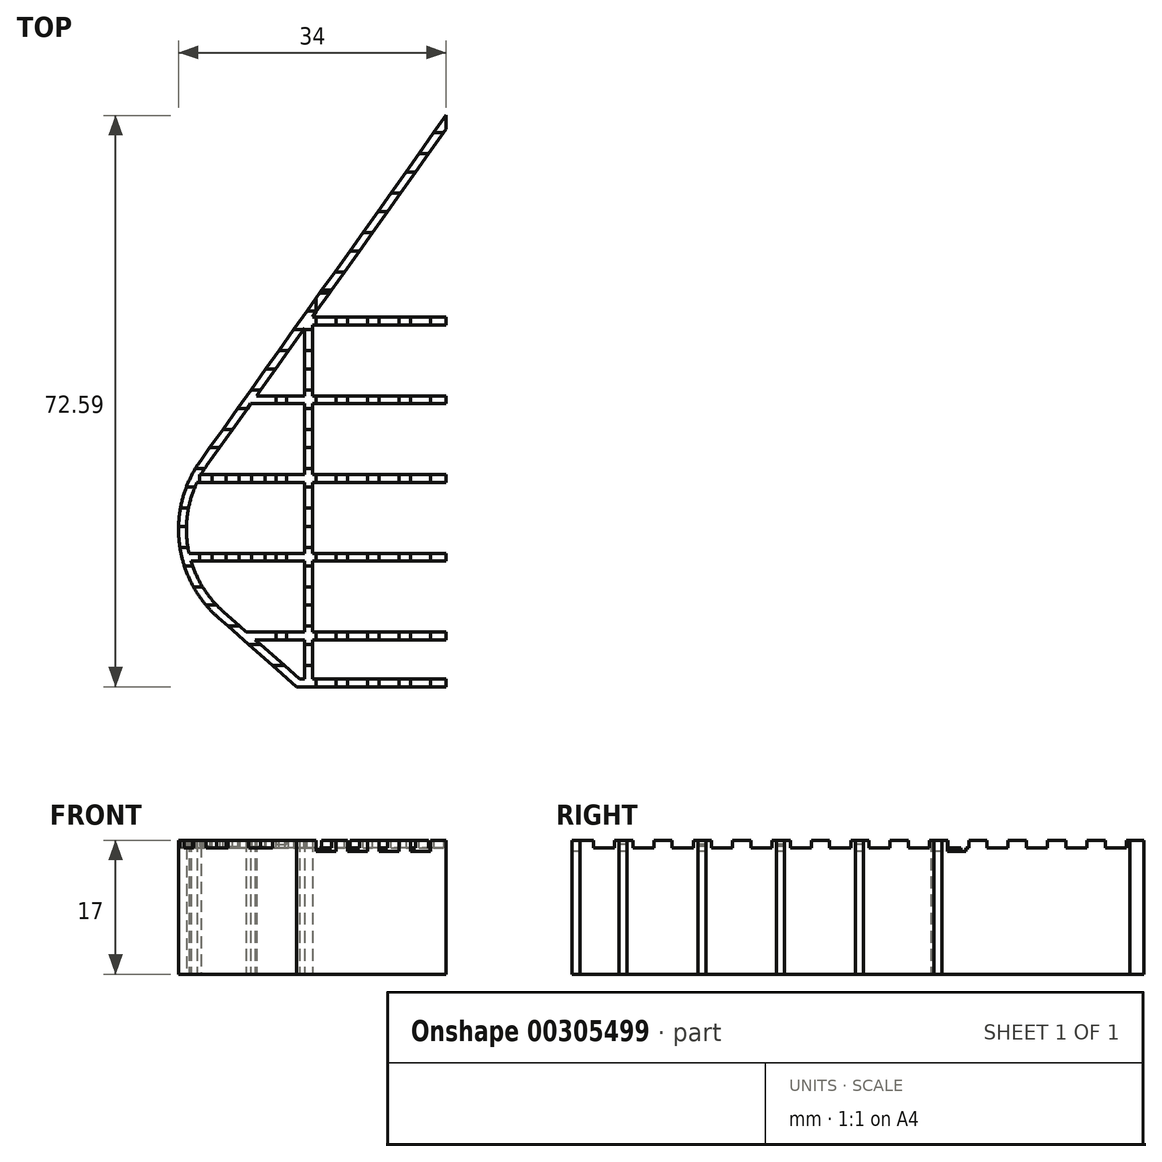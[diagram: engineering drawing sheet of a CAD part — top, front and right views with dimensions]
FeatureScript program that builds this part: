
annotation { "Feature Type Name" : "Feature", "Feature Type Description" : "" }
export const myFeature = defineFeature(function(context is Context, id is Id, definition is map)
    precondition{}
    {
        {
            var Q0;
            Q0=qCreatedBy(makeId("Top.planeOp"),FACE);
            var sketch = newSketch(context, id + "F0", { "sketchPlane" : qUnion([Q0])});
            skLineSegment(sketch, "E0.MirrorCS", {"start": v(-52.18, -20) * mm, "end": v(-53.18, -20) * mm, "construction": true});
            skLineSegment(sketch, "E1.MirrorCS", {"start": v(-53.18, -19) * mm, "end": v(-53.18, -20) * mm});
            skLineSegment(sketch, "E2.MirrorCS", {"start": v(-71.18, -19) * mm, "end": v(-71.8, -19) * mm});
            skLineSegment(sketch, "E3.MirrorCS", {"start": v(-53.18, 52.6) * mm, "end": v(-53.18, 50.87) * mm});
            skLineSegment(sketch, "E4.MirrorCS", {"start": v(-53.18, -19) * mm, "end": v(-70.18, -19) * mm, "construction": true});
            skLineSegment(sketch, "E5.MirrorCS", {"start": v(-71.18, 25.56) * mm, "end": v(-77.3, 16.97) * mm});
            skLineSegment(sketch, "E6.MirrorCS", {"start": v(-70.18, -19) * mm, "end": v(-70.18, -14.03) * mm});
            skLineSegment(sketch, "E7.MirrorCS", {"start": v(-53.18, 50.87) * mm, "end": v(-70.18, 26.97) * mm});
            skLineSegment(sketch, "E8.MirrorCS", {"start": v(-72.18, 0) * mm, "end": v(-52.18, 0) * mm, "construction": true});
            skLineSegment(sketch, "E9.MirrorCS", {"start": v(-52.18, 0) * mm, "end": v(-52.18, 54) * mm, "construction": true});
            skLineSegment(sketch, "E10.MirrorCS", {"start": v(-53.18, -19) * mm, "end": v(-53.18, 56.1) * mm, "construction": true});
            skLineSegment(sketch, "E11.MirrorCS", {"start": v(-52.18, 0) * mm, "end": v(-52.18, -20) * mm, "construction": true});
            skLineSegment(sketch, "E12.MirrorCS", {"start": v(-53.18, -19) * mm, "end": v(-70.18, -19) * mm});
            skLineSegment(sketch, "E13.MirrorCS", {"start": v(-71.8, -19) * mm, "end": v(-77.44, -14.03) * mm});
            skLineSegment(sketch, "E14.MirrorCS", {"start": v(-53.18, 52.6) * mm, "end": v(-84.4, 8.7) * mm});
            skLineSegment(sketch, "E15.MirrorCS", {"start": v(-72.18, -20) * mm, "end": v(-82.1, -11.25) * mm});
            skArc(sketch, "E16.MirrorCS", {"start": v(-82.1, -11.25) * mm, "mid": v(-87.09, -1.72) * mm, "end": v(-84.4, 8.7) * mm});
            skArc(sketch, "E17.MirrorCS", {"start": v(-81.44, -10.5) * mm, "mid": v(-83.97, -7.56) * mm, "end": v(-85.6, -4.03) * mm});
            skLineSegment(sketch, "E18.MirrorCS", {"start": v(-53.18, -20) * mm, "end": v(-72.18, -20) * mm});
            skLineSegment(sketch, "E19.MirrorCS", {"start": v(-71.18, -19) * mm, "end": v(-71.18, -14.03) * mm});
            skLineSegment(sketch, "E20", {"start": v(-70.18, 26.97) * mm, "end": v(-53.18, 26.97) * mm});
            skLineSegment(sketch, "E21", {"start": v(-53.18, 26.97) * mm, "end": v(-53.18, 25.97) * mm});
            skLineSegment(sketch, "E22", {"start": v(-53.18, 25.97) * mm, "end": v(-70.18, 25.97) * mm});
            skLineSegment(sketch, "E23.0.1.0", {"start": v(-70.18, 16.97) * mm, "end": v(-53.18, 16.97) * mm});
            skLineSegment(sketch, "E23.0.1.1", {"start": v(-53.18, 15.97) * mm, "end": v(-70.18, 15.97) * mm});
            skLineSegment(sketch, "E23.0.1.2", {"start": v(-53.18, 16.97) * mm, "end": v(-53.18, 15.97) * mm});
            skLineSegment(sketch, "E23.0.2.0", {"start": v(-70.18, 6.97) * mm, "end": v(-53.18, 6.97) * mm});
            skLineSegment(sketch, "E23.0.2.1", {"start": v(-53.18, 5.97) * mm, "end": v(-70.18, 5.97) * mm});
            skLineSegment(sketch, "E23.0.2.2", {"start": v(-53.18, 6.97) * mm, "end": v(-53.18, 5.97) * mm});
            skLineSegment(sketch, "E23.0.3.0", {"start": v(-70.18, -3.03) * mm, "end": v(-53.18, -3.03) * mm});
            skLineSegment(sketch, "E23.0.3.1", {"start": v(-53.18, -4.03) * mm, "end": v(-70.18, -4.03) * mm});
            skLineSegment(sketch, "E23.0.3.2", {"start": v(-53.18, -3.03) * mm, "end": v(-53.18, -4.03) * mm});
            skLineSegment(sketch, "E23.0.4.0", {"start": v(-70.18, -13.03) * mm, "end": v(-53.18, -13.03) * mm});
            skLineSegment(sketch, "E23.0.4.1", {"start": v(-53.18, -14.03) * mm, "end": v(-70.18, -14.03) * mm});
            skLineSegment(sketch, "E23.0.4.2", {"start": v(-53.18, -13.03) * mm, "end": v(-53.18, -14.03) * mm});
            skLineSegment(sketch, "E23.direction1", {"start": v(-70.18, 25.97) * mm, "end": v(-45.18, 25.97) * mm, "construction": true});
            skLineSegment(sketch, "E23.direction2", {"start": v(-70.18, 25.97) * mm, "end": v(-70.18, 16.97) * mm, "construction": true});
            skLineSegment(sketch, "E24.trimOffspring", {"start": v(-70.18, 16.97) * mm, "end": v(-70.18, 25.97) * mm});
            skLineSegment(sketch, "E25.trimOffspring", {"start": v(-70.18, 6.97) * mm, "end": v(-70.18, 15.97) * mm});
            skLineSegment(sketch, "E26.trimOffspring", {"start": v(-70.18, -3.03) * mm, "end": v(-70.18, 5.97) * mm});
            skLineSegment(sketch, "E27.trimOffspring", {"start": v(-70.18, -13.03) * mm, "end": v(-70.18, -4.03) * mm});
            skLineSegment(sketch, "E28", {"start": v(-71.18, 16.97) * mm, "end": v(-77.3, 16.97) * mm});
            skLineSegment(sketch, "E29", {"start": v(-71.18, 6.97) * mm, "end": v(-84.33, 6.97) * mm});
            skLineSegment(sketch, "E30", {"start": v(-71.18, -3.03) * mm, "end": v(-85.85, -3.03) * mm});
            skLineSegment(sketch, "E31", {"start": v(-71.18, -13.03) * mm, "end": v(-78.57, -13.03) * mm});
            skLineSegment(sketch, "E32.0", {"start": v(-71.18, 15.97) * mm, "end": v(-78, 15.97) * mm});
            skLineSegment(sketch, "E33.0", {"start": v(-71.18, 5.97) * mm, "end": v(-84.85, 5.97) * mm});
            skLineSegment(sketch, "E34.0", {"start": v(-71.18, -4.03) * mm, "end": v(-85.6, -4.03) * mm});
            skLineSegment(sketch, "E35.0", {"start": v(-71.18, -14.03) * mm, "end": v(-77.44, -14.03) * mm});
            skLineSegment(sketch, "E36.trimOffspring", {"start": v(-71.18, 6.97) * mm, "end": v(-71.18, 15.97) * mm});
            skLineSegment(sketch, "E37.trimOffspring", {"start": v(-71.18, 16.97) * mm, "end": v(-71.18, 25.56) * mm});
            skLineSegment(sketch, "E38.trimOffspring", {"start": v(-71.18, -3.03) * mm, "end": v(-71.18, 5.97) * mm});
            skLineSegment(sketch, "E39.trimOffspring", {"start": v(-71.18, -13.03) * mm, "end": v(-71.18, -4.03) * mm});
            skLineSegment(sketch, "E40.trimOffspring", {"start": v(-78, 15.97) * mm, "end": v(-83.6, 8.11) * mm});
            skArc(sketch, "E41.trimOffspring", {"start": v(-84.33, 6.97) * mm, "mid": v(-83.97, 7.55) * mm, "end": v(-83.6, 8.11) * mm});
            skArc(sketch, "E42.trimOffspring", {"start": v(-85.85, -3.03) * mm, "mid": v(-86.1, 1.55) * mm, "end": v(-84.85, 5.97) * mm});
            skLineSegment(sketch, "E43.trimOffspring", {"start": v(-78.57, -13.03) * mm, "end": v(-81.44, -10.5) * mm});
            skSolve(sketch);
        }
        {
            var Q0;
            Q0=makeQuery(id+"F0.imprint","IMPRINT",FACE,{"disambiguationData":[TD([[makeQuery(id+"F0.imprint","IMPRINT",EDGE,{"derivedFrom":sQuery(id+"F0.wireOp",EDGE,"E1.MirrorCS")}),-1.0]])]});
            extrude(context, id + "F1", {"entities" : qUnion([Q0]), "endBound" : BoundingType.SYMMETRIC, "depth" : 17 * mm});
        }
        {
            var Q0;
            Q0=qCreatedBy(makeId("Right.planeOp"),FACE);
            var sketch = newSketch(context, id + "F2", { "sketchPlane" : qUnion([Q0])});
            skLineSegment(sketch, "E44", {"start": v(50.38, 9.62) * mm, "end": v(50.38, 7.56) * mm});
            skLineSegment(sketch, "E45", {"start": v(50.38, 7.56) * mm, "end": v(47.7, 7.56) * mm});
            skLineSegment(sketch, "E46", {"start": v(47.7, 7.56) * mm, "end": v(47.7, 9.62) * mm});
            skLineSegment(sketch, "E47", {"start": v(47.7, 9.62) * mm, "end": v(50.38, 9.62) * mm});
            skLineSegment(sketch, "E48.1.0.0", {"start": v(42.7, 7.56) * mm, "end": v(42.7, 9.62) * mm});
            skLineSegment(sketch, "E48.1.0.1", {"start": v(42.7, 9.62) * mm, "end": v(45.38, 9.62) * mm});
            skLineSegment(sketch, "E48.1.0.2", {"start": v(45.38, 7.56) * mm, "end": v(42.7, 7.56) * mm});
            skLineSegment(sketch, "E48.1.0.3", {"start": v(45.38, 9.62) * mm, "end": v(45.38, 7.56) * mm});
            skLineSegment(sketch, "E48.2.0.0", {"start": v(37.7, 7.56) * mm, "end": v(37.7, 9.62) * mm});
            skLineSegment(sketch, "E48.2.0.1", {"start": v(37.7, 9.62) * mm, "end": v(40.38, 9.62) * mm});
            skLineSegment(sketch, "E48.2.0.2", {"start": v(40.38, 7.56) * mm, "end": v(37.7, 7.56) * mm});
            skLineSegment(sketch, "E48.2.0.3", {"start": v(40.38, 9.62) * mm, "end": v(40.38, 7.56) * mm});
            skLineSegment(sketch, "E48.3.0.0", {"start": v(32.7, 7.56) * mm, "end": v(32.7, 9.62) * mm});
            skLineSegment(sketch, "E48.3.0.1", {"start": v(32.7, 9.62) * mm, "end": v(35.38, 9.62) * mm});
            skLineSegment(sketch, "E48.3.0.2", {"start": v(35.38, 7.56) * mm, "end": v(32.7, 7.56) * mm});
            skLineSegment(sketch, "E48.3.0.3", {"start": v(35.38, 9.62) * mm, "end": v(35.38, 7.56) * mm});
            skLineSegment(sketch, "E48.4.0.0", {"start": v(27.7, 7.56) * mm, "end": v(27.7, 9.62) * mm});
            skLineSegment(sketch, "E48.4.0.1", {"start": v(27.7, 9.62) * mm, "end": v(30.38, 9.62) * mm});
            skLineSegment(sketch, "E48.4.0.2", {"start": v(30.38, 7.56) * mm, "end": v(27.7, 7.56) * mm});
            skLineSegment(sketch, "E48.4.0.3", {"start": v(30.38, 9.62) * mm, "end": v(30.38, 7.56) * mm});
            skLineSegment(sketch, "E48.5.0.0", {"start": v(22.7, 7.56) * mm, "end": v(22.7, 9.62) * mm});
            skLineSegment(sketch, "E48.5.0.1", {"start": v(22.7, 9.62) * mm, "end": v(25.38, 9.62) * mm});
            skLineSegment(sketch, "E48.5.0.2", {"start": v(25.38, 7.56) * mm, "end": v(22.7, 7.56) * mm});
            skLineSegment(sketch, "E48.5.0.3", {"start": v(25.38, 9.62) * mm, "end": v(25.38, 7.56) * mm});
            skLineSegment(sketch, "E48.6.0.0", {"start": v(17.7, 7.56) * mm, "end": v(17.7, 9.62) * mm});
            skLineSegment(sketch, "E48.6.0.1", {"start": v(17.7, 9.62) * mm, "end": v(20.38, 9.62) * mm});
            skLineSegment(sketch, "E48.6.0.2", {"start": v(20.38, 7.56) * mm, "end": v(17.7, 7.56) * mm});
            skLineSegment(sketch, "E48.6.0.3", {"start": v(20.38, 9.62) * mm, "end": v(20.38, 7.56) * mm});
            skLineSegment(sketch, "E48.7.0.0", {"start": v(12.7, 7.56) * mm, "end": v(12.7, 9.62) * mm});
            skLineSegment(sketch, "E48.7.0.1", {"start": v(12.7, 9.62) * mm, "end": v(15.38, 9.62) * mm});
            skLineSegment(sketch, "E48.7.0.2", {"start": v(15.38, 7.56) * mm, "end": v(12.7, 7.56) * mm});
            skLineSegment(sketch, "E48.7.0.3", {"start": v(15.38, 9.62) * mm, "end": v(15.38, 7.56) * mm});
            skLineSegment(sketch, "E48.8.0.0", {"start": v(7.7, 7.56) * mm, "end": v(7.7, 9.62) * mm});
            skLineSegment(sketch, "E48.8.0.1", {"start": v(7.7, 9.62) * mm, "end": v(10.38, 9.62) * mm});
            skLineSegment(sketch, "E48.8.0.2", {"start": v(10.38, 7.56) * mm, "end": v(7.7, 7.56) * mm});
            skLineSegment(sketch, "E48.8.0.3", {"start": v(10.38, 9.62) * mm, "end": v(10.38, 7.56) * mm});
            skLineSegment(sketch, "E48.9.0.0", {"start": v(2.7, 7.56) * mm, "end": v(2.7, 9.62) * mm});
            skLineSegment(sketch, "E48.9.0.1", {"start": v(2.7, 9.62) * mm, "end": v(5.38, 9.62) * mm});
            skLineSegment(sketch, "E48.9.0.2", {"start": v(5.38, 7.56) * mm, "end": v(2.7, 7.56) * mm});
            skLineSegment(sketch, "E48.9.0.3", {"start": v(5.38, 9.62) * mm, "end": v(5.38, 7.56) * mm});
            skLineSegment(sketch, "E48.10.0.0", {"start": v(-2.3, 7.56) * mm, "end": v(-2.3, 9.62) * mm});
            skLineSegment(sketch, "E48.10.0.1", {"start": v(-2.3, 9.62) * mm, "end": v(0.38, 9.62) * mm});
            skLineSegment(sketch, "E48.10.0.2", {"start": v(0.38, 7.56) * mm, "end": v(-2.3, 7.56) * mm});
            skLineSegment(sketch, "E48.10.0.3", {"start": v(0.38, 9.62) * mm, "end": v(0.38, 7.56) * mm});
            skLineSegment(sketch, "E48.11.0.0", {"start": v(-7.3, 7.56) * mm, "end": v(-7.3, 9.62) * mm});
            skLineSegment(sketch, "E48.11.0.1", {"start": v(-7.3, 9.62) * mm, "end": v(-4.62, 9.62) * mm});
            skLineSegment(sketch, "E48.11.0.2", {"start": v(-4.62, 7.56) * mm, "end": v(-7.3, 7.56) * mm});
            skLineSegment(sketch, "E48.11.0.3", {"start": v(-4.62, 9.62) * mm, "end": v(-4.62, 7.56) * mm});
            skLineSegment(sketch, "E48.12.0.0", {"start": v(-12.3, 7.56) * mm, "end": v(-12.3, 9.62) * mm});
            skLineSegment(sketch, "E48.12.0.1", {"start": v(-12.3, 9.62) * mm, "end": v(-9.62, 9.62) * mm});
            skLineSegment(sketch, "E48.12.0.2", {"start": v(-9.62, 7.56) * mm, "end": v(-12.3, 7.56) * mm});
            skLineSegment(sketch, "E48.12.0.3", {"start": v(-9.62, 9.62) * mm, "end": v(-9.62, 7.56) * mm});
            skLineSegment(sketch, "E48.13.0.0", {"start": v(-17.3, 7.56) * mm, "end": v(-17.3, 9.62) * mm});
            skLineSegment(sketch, "E48.13.0.1", {"start": v(-17.3, 9.62) * mm, "end": v(-14.62, 9.62) * mm});
            skLineSegment(sketch, "E48.13.0.2", {"start": v(-14.62, 7.56) * mm, "end": v(-17.3, 7.56) * mm});
            skLineSegment(sketch, "E48.13.0.3", {"start": v(-14.62, 9.62) * mm, "end": v(-14.62, 7.56) * mm});
            skLineSegment(sketch, "E48.direction1", {"start": v(47.7, 7.56) * mm, "end": v(42.7, 7.56) * mm, "construction": true});
            skSolve(sketch);
        }
        {
            var Q0;
            Q0=makeQuery(id+"F2.imprint","IMPRINT",FACE,{"disambiguationData":[TD([[makeQuery(id+"F2.imprint","IMPRINT",EDGE,{"derivedFrom":sQuery(id+"F2.wireOp",EDGE,"E44")}),-1.0]])]});
            var Q1;
            Q1=makeQuery(id+"F2.imprint","IMPRINT",FACE,{"disambiguationData":[TD([[makeQuery(id+"F2.imprint","IMPRINT",EDGE,{"derivedFrom":sQuery(id+"F2.wireOp",EDGE,"E48.1.0.0")}),-1.0]])]});
            var Q2;
            Q2=makeQuery(id+"F2.imprint","IMPRINT",FACE,{"disambiguationData":[TD([[makeQuery(id+"F2.imprint","IMPRINT",EDGE,{"derivedFrom":sQuery(id+"F2.wireOp",EDGE,"E48.2.0.0")}),-1.0]])]});
            var Q3;
            Q3=makeQuery(id+"F2.imprint","IMPRINT",FACE,{"disambiguationData":[TD([[makeQuery(id+"F2.imprint","IMPRINT",EDGE,{"derivedFrom":sQuery(id+"F2.wireOp",EDGE,"E48.13.0.0")}),-1.0]])]});
            var Q4;
            Q4=makeQuery(id+"F2.imprint","IMPRINT",FACE,{"disambiguationData":[TD([[makeQuery(id+"F2.imprint","IMPRINT",EDGE,{"derivedFrom":sQuery(id+"F2.wireOp",EDGE,"E48.3.0.0")}),-1.0]])]});
            var Q5;
            Q5=makeQuery(id+"F2.imprint","IMPRINT",FACE,{"disambiguationData":[TD([[makeQuery(id+"F2.imprint","IMPRINT",EDGE,{"derivedFrom":sQuery(id+"F2.wireOp",EDGE,"E48.4.0.0")}),-1.0]])]});
            var Q6;
            Q6=makeQuery(id+"F2.imprint","IMPRINT",FACE,{"disambiguationData":[TD([[makeQuery(id+"F2.imprint","IMPRINT",EDGE,{"derivedFrom":sQuery(id+"F2.wireOp",EDGE,"E48.5.0.0")}),-1.0]])]});
            var Q7;
            Q7=makeQuery(id+"F2.imprint","IMPRINT",FACE,{"disambiguationData":[TD([[makeQuery(id+"F2.imprint","IMPRINT",EDGE,{"derivedFrom":sQuery(id+"F2.wireOp",EDGE,"E48.6.0.0")}),-1.0]])]});
            var Q8;
            Q8=makeQuery(id+"F2.imprint","IMPRINT",FACE,{"disambiguationData":[TD([[makeQuery(id+"F2.imprint","IMPRINT",EDGE,{"derivedFrom":sQuery(id+"F2.wireOp",EDGE,"E48.7.0.0")}),-1.0]])]});
            var Q9;
            Q9=makeQuery(id+"F2.imprint","IMPRINT",FACE,{"disambiguationData":[TD([[makeQuery(id+"F2.imprint","IMPRINT",EDGE,{"derivedFrom":sQuery(id+"F2.wireOp",EDGE,"E48.8.0.0")}),-1.0]])]});
            var Q10;
            Q10=makeQuery(id+"F2.imprint","IMPRINT",FACE,{"disambiguationData":[TD([[makeQuery(id+"F2.imprint","IMPRINT",EDGE,{"derivedFrom":sQuery(id+"F2.wireOp",EDGE,"E48.9.0.0")}),-1.0]])]});
            var Q11;
            Q11=makeQuery(id+"F2.imprint","IMPRINT",FACE,{"disambiguationData":[TD([[makeQuery(id+"F2.imprint","IMPRINT",EDGE,{"derivedFrom":sQuery(id+"F2.wireOp",EDGE,"E48.10.0.0")}),-1.0]])]});
            var Q12;
            Q12=makeQuery(id+"F2.imprint","IMPRINT",FACE,{"disambiguationData":[TD([[makeQuery(id+"F2.imprint","IMPRINT",EDGE,{"derivedFrom":sQuery(id+"F2.wireOp",EDGE,"E48.11.0.0")}),-1.0]])]});
            var Q13;
            Q13=makeQuery(id+"F2.imprint","IMPRINT",FACE,{"disambiguationData":[TD([[makeQuery(id+"F2.imprint","IMPRINT",EDGE,{"derivedFrom":sQuery(id+"F2.wireOp",EDGE,"E48.12.0.0")}),-1.0]])]});
            extrude(context, id + "F3", {"entities" : qUnion([Q0, Q1, Q2, Q3, Q4, Q5, Q6, Q7, Q8, Q9, Q10, Q11, Q12, Q13]), "operationType" : NewBodyOperationType.REMOVE, "endBound" : BoundingType.THROUGH_ALL, "oppositeDirection" : true, "depth" : 25 * mm});
        }
        {
            var Q0;
            Q0=makeQuery(id+"F1.opExtrude","SWEPT_FACE",FACE,{"disambiguationData":[OSD([sQuery(id+"F0.wireOp",EDGE,"E18.MirrorCS")])]});
            var sketch = newSketch(context, id + "F4", { "sketchPlane" : qUnion([Q0])});
            skLineSegment(sketch, "E49", {"start": v(-69.68, 9.94) * mm, "end": v(-69.68, 7.1) * mm});
            skLineSegment(sketch, "E50", {"start": v(-69.68, 7.1) * mm, "end": v(-67.2, 7.1) * mm});
            skLineSegment(sketch, "E51", {"start": v(-67.2, 7.1) * mm, "end": v(-67.2, 9.85) * mm});
            skLineSegment(sketch, "E52", {"start": v(-67.2, 9.85) * mm, "end": v(-69.68, 9.94) * mm});
            skLineSegment(sketch, "E53.1.0.0", {"start": v(-63.2, 7.1) * mm, "end": v(-63.2, 9.85) * mm});
            skLineSegment(sketch, "E53.1.0.1", {"start": v(-63.2, 9.85) * mm, "end": v(-65.68, 9.94) * mm});
            skLineSegment(sketch, "E53.1.0.2", {"start": v(-65.68, 7.1) * mm, "end": v(-63.2, 7.1) * mm});
            skLineSegment(sketch, "E53.1.0.3", {"start": v(-65.68, 9.94) * mm, "end": v(-65.68, 7.1) * mm});
            skLineSegment(sketch, "E53.2.0.0", {"start": v(-59.2, 7.1) * mm, "end": v(-59.2, 9.85) * mm});
            skLineSegment(sketch, "E53.2.0.1", {"start": v(-59.2, 9.85) * mm, "end": v(-61.68, 9.94) * mm});
            skLineSegment(sketch, "E53.2.0.2", {"start": v(-61.68, 7.1) * mm, "end": v(-59.2, 7.1) * mm});
            skLineSegment(sketch, "E53.2.0.3", {"start": v(-61.68, 9.94) * mm, "end": v(-61.68, 7.1) * mm});
            skLineSegment(sketch, "E53.3.0.0", {"start": v(-55.2, 7.1) * mm, "end": v(-55.2, 9.85) * mm});
            skLineSegment(sketch, "E53.3.0.1", {"start": v(-55.2, 9.85) * mm, "end": v(-57.68, 9.94) * mm});
            skLineSegment(sketch, "E53.3.0.2", {"start": v(-57.68, 7.1) * mm, "end": v(-55.2, 7.1) * mm});
            skLineSegment(sketch, "E53.3.0.3", {"start": v(-57.68, 9.94) * mm, "end": v(-57.68, 7.1) * mm});
            skLineSegment(sketch, "E53.direction1", {"start": v(-69.68, 7.1) * mm, "end": v(-65.68, 7.1) * mm, "construction": true});
            skSolve(sketch);
        }
        {
            var Q0;
            {var subQ0=sQuery(id+"F4.wireOp",EDGE,"E50");Q0=makeQuery(id+"F4.imprint","IMPRINT",FACE,{"disambiguationData":[TD([[makeQuery(id+"F4.imprint","IMPRINT",EDGE,{"derivedFrom":subQ0}),1.0]])]});}
            var Q1;
            {var subQ0=sQuery(id+"F4.wireOp",EDGE,"E53.1.0.2");Q1=makeQuery(id+"F4.imprint","IMPRINT",FACE,{"disambiguationData":[TD([[makeQuery(id+"F4.imprint","IMPRINT",EDGE,{"derivedFrom":subQ0}),1.0]])]});}
            var Q2;
            {var subQ0=sQuery(id+"F4.wireOp",EDGE,"E53.2.0.2");Q2=makeQuery(id+"F4.imprint","IMPRINT",FACE,{"disambiguationData":[TD([[makeQuery(id+"F4.imprint","IMPRINT",EDGE,{"derivedFrom":subQ0}),1.0]])]});}
            var Q3;
            {var subQ0=sQuery(id+"F4.wireOp",EDGE,"E53.3.0.2");Q3=makeQuery(id+"F4.imprint","IMPRINT",FACE,{"disambiguationData":[TD([[makeQuery(id+"F4.imprint","IMPRINT",EDGE,{"derivedFrom":subQ0}),1.0]])]});}
            extrude(context, id + "F5", {"entities" : qUnion([Q0, Q1, Q2, Q3]), "operationType" : NewBodyOperationType.REMOVE, "oppositeDirection" : true, "depth" : 50 * mm});
        }
        {
            var Q0;
            Q0=makeQuery(id+"F1.opExtrude","SWEPT_FACE",FACE,{"disambiguationData":[OSD([sQuery(id+"F0.wireOp",EDGE,"E35.0")])]});
            var sketch = newSketch(context, id + "F6", { "sketchPlane" : qUnion([Q0])});
            skLineSegment(sketch, "E54", {"start": v(-74.82, 9.11) * mm, "end": v(-74.82, 7.96) * mm});
            skLineSegment(sketch, "E55", {"start": v(-74.82, 7.96) * mm, "end": v(-73.45, 7.96) * mm});
            skLineSegment(sketch, "E56", {"start": v(-73.45, 7.96) * mm, "end": v(-73.45, 9.2) * mm});
            skLineSegment(sketch, "E57", {"start": v(-73.45, 9.2) * mm, "end": v(-74.82, 9.11) * mm});
            skSolve(sketch);
        }
        {
            var Q0;
            {var subQ0=sQuery(id+"F6.wireOp",EDGE,"E55");Q0=makeQuery(id+"F6.imprint","IMPRINT",FACE,{"disambiguationData":[TD([[makeQuery(id+"F6.imprint","IMPRINT",EDGE,{"derivedFrom":subQ0}),1.0]])]});}
            extrude(context, id + "F7", {"entities" : qUnion([Q0]), "operationType" : NewBodyOperationType.REMOVE, "oppositeDirection" : true, "depth" : 32 * mm});
        }
        {
            var Q0;
            Q0=makeQuery(id+"F1.opExtrude","SWEPT_FACE",FACE,{"disambiguationData":[OSD([sQuery(id+"F0.wireOp",EDGE,"E34.0")])]});
            var sketch = newSketch(context, id + "F8", { "sketchPlane" : qUnion([Q0])});
            skLineSegment(sketch, "E58", {"start": v(-84.52, 9.15) * mm, "end": v(-84.52, 7.8) * mm});
            skLineSegment(sketch, "E59", {"start": v(-84.52, 7.8) * mm, "end": v(-82.94, 7.8) * mm});
            skLineSegment(sketch, "E60", {"start": v(-82.94, 7.8) * mm, "end": v(-82.94, 9.17) * mm});
            skLineSegment(sketch, "E61", {"start": v(-82.94, 9.17) * mm, "end": v(-84.52, 9.15) * mm});
            skLineSegment(sketch, "E62", {"start": v(-81.14, 9.16) * mm, "end": v(-81.14, 7.72) * mm});
            skLineSegment(sketch, "E63", {"start": v(-81.14, 7.72) * mm, "end": v(-79.48, 7.72) * mm});
            skLineSegment(sketch, "E64", {"start": v(-79.48, 7.72) * mm, "end": v(-79.48, 9.18) * mm});
            skLineSegment(sketch, "E65", {"start": v(-79.48, 9.18) * mm, "end": v(-81.14, 9.16) * mm});
            skLineSegment(sketch, "E66", {"start": v(-77.88, 9.24) * mm, "end": v(-77.88, 7.72) * mm});
            skLineSegment(sketch, "E67", {"start": v(-77.88, 7.72) * mm, "end": v(-76.19, 7.72) * mm});
            skLineSegment(sketch, "E68", {"start": v(-76.19, 7.72) * mm, "end": v(-76.19, 9.21) * mm});
            skLineSegment(sketch, "E69", {"start": v(-76.19, 9.21) * mm, "end": v(-77.88, 9.24) * mm});
            skSolve(sketch);
        }
        {
            var Q0;
            {var subQ0=sQuery(id+"F8.wireOp",EDGE,"E59");Q0=makeQuery(id+"F8.imprint","IMPRINT",FACE,{"disambiguationData":[TD([[makeQuery(id+"F8.imprint","IMPRINT",EDGE,{"derivedFrom":subQ0}),1.0]])]});}
            var Q1;
            {var subQ0=sQuery(id+"F8.wireOp",EDGE,"E67");Q1=makeQuery(id+"F8.imprint","IMPRINT",FACE,{"disambiguationData":[TD([[makeQuery(id+"F8.imprint","IMPRINT",EDGE,{"derivedFrom":subQ0}),1.0]])]});}
            var Q2;
            {var subQ0=sQuery(id+"F8.wireOp",EDGE,"E63");Q2=makeQuery(id+"F8.imprint","IMPRINT",FACE,{"disambiguationData":[TD([[makeQuery(id+"F8.imprint","IMPRINT",EDGE,{"derivedFrom":subQ0}),1.0]])]});}
            extrude(context, id + "F9", {"entities" : qUnion([Q0, Q1, Q2]), "operationType" : NewBodyOperationType.REMOVE, "oppositeDirection" : true, "depth" : 11 * mm});
        }
    });
